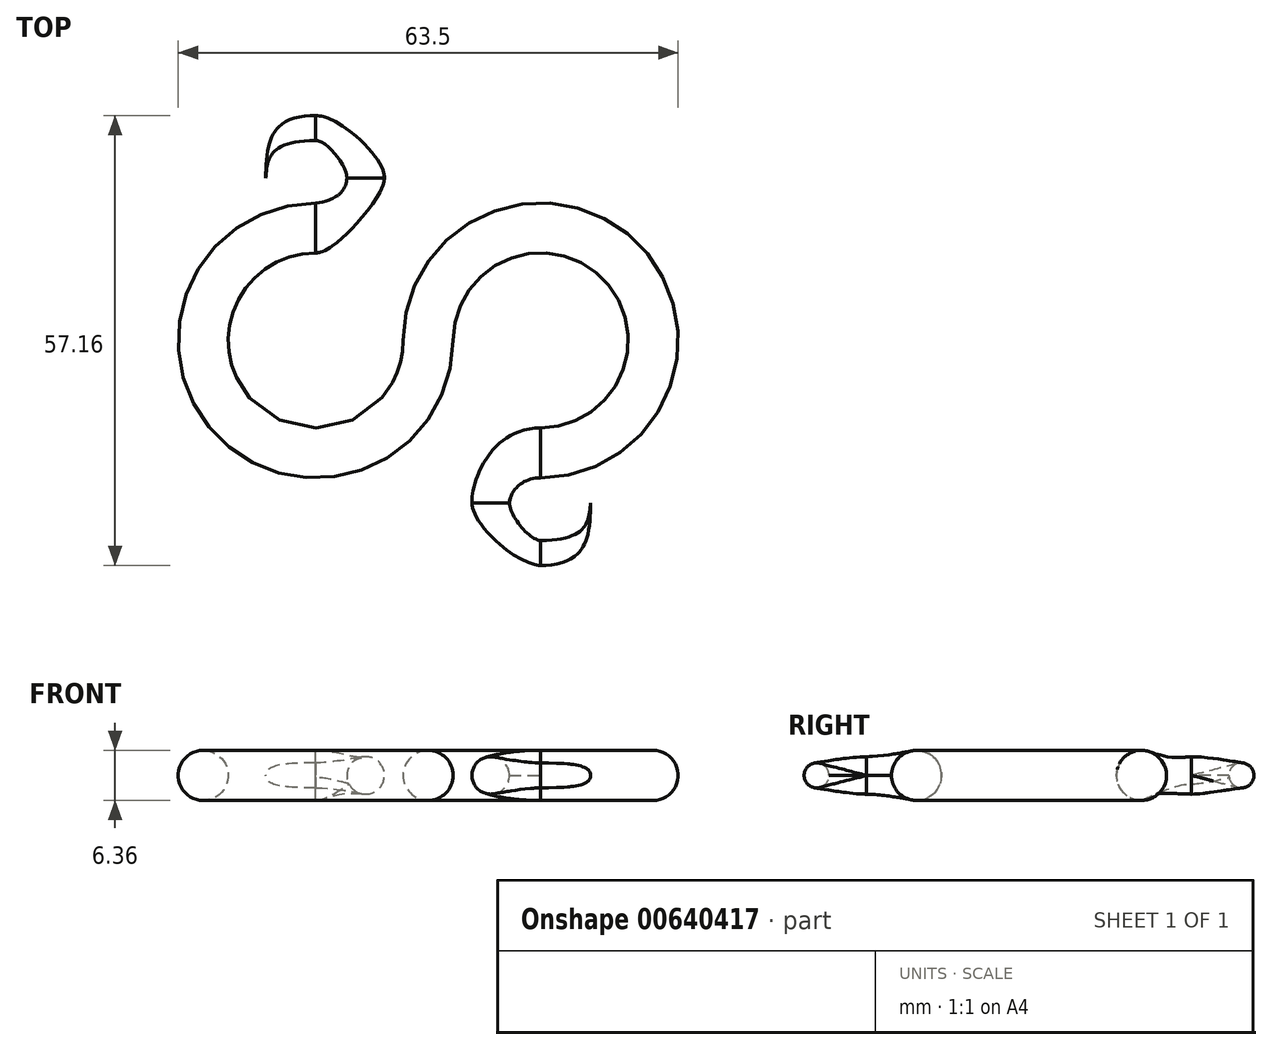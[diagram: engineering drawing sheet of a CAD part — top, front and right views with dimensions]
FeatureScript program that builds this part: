
annotation { "Feature Type Name" : "Feature", "Feature Type Description" : "" }
export const myFeature = defineFeature(function(context is Context, id is Id, definition is map)
    precondition{}
    {
        {
            var Q0;
            Q0=qCreatedBy(makeId("Top.planeOp"),FACE);
            var sketch = newSketch(context, id + "F0", { "sketchPlane" : qUnion([Q0])});
            skArc(sketch, "E0", {"start": v(0, -14.29) * mm, "mid": v(-6.35, -20.64) * mm, "end": v(0, -26.99) * mm});
            skArc(sketch, "E1", {"start": v(0, -14.29) * mm, "mid": v(10.1, 10.1) * mm, "end": v(-14.29, 0) * mm});
            skLineSegment(sketch, "E2", {"start": v(0, 0) * mm, "end": v(-14.29, 0) * mm, "construction": true});
            skLineSegment(sketch, "E3", {"start": v(0, 0) * mm, "end": v(0, -14.29) * mm, "construction": true});
            skArc(sketch, "E4", {"start": v(-28.58, 14.29) * mm, "mid": v(-38.68, -10.1) * mm, "end": v(-14.29, 0) * mm});
            skArc(sketch, "E5", {"start": v(-28.58, 14.29) * mm, "mid": v(-22.22, 20.64) * mm, "end": v(-28.57, 26.99) * mm});
            skArc(sketch, "E6", {"start": v(0, -26.99) * mm, "mid": v(4.5, -25.13) * mm, "end": v(6.35, -20.64) * mm});
            skArc(sketch, "E7", {"start": v(-28.57, 26.99) * mm, "mid": v(-33.07, 25.13) * mm, "end": v(-34.93, 20.64) * mm});
            skLineSegment(sketch, "E8", {"start": v(0, -20.64) * mm, "end": v(6.35, -20.64) * mm, "construction": true});
            skLineSegment(sketch, "E9", {"start": v(0, -20.64) * mm, "end": v(0, -26.99) * mm, "construction": true});
            skLineSegment(sketch, "E10", {"start": v(-34.92, 20.64) * mm, "end": v(-28.58, 20.64) * mm, "construction": true});
            skLineSegment(sketch, "E11", {"start": v(-28.58, 26.99) * mm, "end": v(-28.57, 20.64) * mm, "construction": true});
            skSolve(sketch);
        }
        {
            var Q0;
            Q0=sQuery(id+"F0.wireOp",EDGE,"E0");
            cPlane(context, id + "F1", {"entities" : qUnion([Q0]), "cplaneType" : CPlaneType.MID_PLANE, "offset" : 25.4 * mm, "width" : 152.4 * mm, "height" : 152.4 * mm});
        }
        {
            var Q0;
            Q0=qCreatedBy(makeId("Right.planeOp"),FACE);
            var sketch = newSketch(context, id + "F2", { "sketchPlane" : qUnion([Q0])});
            skCircle(sketch, "E12", {"center": v(-14.29, 0) * mm, "radius": 3.17 * mm});
            skCircle(sketch, "E13", {"center": v(-26.99, 0) * mm, "radius": 1.59 * mm});
            skSolve(sketch);
        }
        {
            var Q0;
            Q0=qCreatedBy(id+"F1.planeOp",FACE);
            var sketch = newSketch(context, id + "F3", { "sketchPlane" : qUnion([Q0])});
            skCircle(sketch, "E14", {"center": v(-6.35, 0) * mm, "radius": 2.38 * mm});
            skSolve(sketch);
        }
        {
            var Q0;
            Q0=makeQuery(id+"F3.imprint","IMPRINT",FACE,{"disambiguationData":[TD([[makeQuery(id+"F3.imprint","IMPRINT",EDGE,{"derivedFrom":sQuery(id+"F3.wireOp",EDGE,"E14")}),1.0]])]});
            var Q1;
            Q1=makeQuery(id+"F2.imprint","IMPRINT",FACE,{"disambiguationData":[TD([[makeQuery(id+"F2.imprint","IMPRINT",EDGE,{"derivedFrom":sQuery(id+"F2.wireOp",EDGE,"E13")}),1.0]])]});
            var Q2;
            Q2=sQuery(id+"F0.wireOp",EDGE,"E0");
            loft(context, id + "F4", {"startCondition" : LoftEndDerivativeType.NORMAL_TO_PROFILE, "startMagnitude" : 1, "endCondition" : LoftEndDerivativeType.NORMAL_TO_PROFILE, "endMagnitude" : 1, "sheetProfilesArray" : [{ "sheetProfileEntities" : qUnion([Q0]) }, { "sheetProfileEntities" : qUnion([Q1]) }], "guidesArray" : [{ "guideEntities" : qUnion([Q2]), "guideDerivativeType" : LoftGuideDerivativeType.DEFAULT, "guideDerivativeMagnitude" : 1 }]});
        }
        {
            var Q1;
            Q1=makeQuery(id+"F4.opLoft","CAP_FACE",FACE,{"disambiguationData":[OSD([makeQuery(id+"F3.imprint","IMPRINT",FACE,{"disambiguationData":[TD([[makeQuery(id+"F3.imprint","IMPRINT",EDGE,{"derivedFrom":sQuery(id+"F3.wireOp",EDGE,"E14")}),1.0]])]})])],"isStart":true});
            var Q2;
            Q2=makeQuery(id+"F2.imprint","IMPRINT",FACE,{"disambiguationData":[TD([[makeQuery(id+"F2.imprint","IMPRINT",EDGE,{"derivedFrom":sQuery(id+"F2.wireOp",EDGE,"E12")}),1.0]])]});
            loft(context, id + "F5", {"operationType" : NewBodyOperationType.ADD, "startCondition" : LoftEndDerivativeType.NORMAL_TO_PROFILE, "startMagnitude" : 1, "endCondition" : LoftEndDerivativeType.NORMAL_TO_PROFILE, "endMagnitude" : 2, "sheetProfilesArray" : [{ "sheetProfileEntities" : qUnion([Q1]) }, { "sheetProfileEntities" : qUnion([Q2]) }]});
        }
        {
            var Q0;
            Q0=makeQuery(id+"F2.imprint","IMPRINT",FACE,{"disambiguationData":[TD([[makeQuery(id+"F2.imprint","IMPRINT",EDGE,{"derivedFrom":sQuery(id+"F2.wireOp",EDGE,"E13")}),1.0]])]});
            var Q1;
            Q1=sQuery(id+"F0.wireOp",VERTEX,"E6.end");
            loft(context, id + "F6", {"operationType" : NewBodyOperationType.ADD, "startCondition" : LoftEndDerivativeType.NORMAL_TO_PROFILE, "startMagnitude" : 2.75, "sheetProfilesArray" : [{ "sheetProfileEntities" : qUnion([Q0]) }, { "sheetProfileEntities" : qUnion([Q1]) }]});
        }
        {
            var Q0;
            Q0=sQuery(id+"F0.wireOp",EDGE,"E5");
            cPlane(context, id + "F7", {"entities" : qUnion([Q0]), "cplaneType" : CPlaneType.MID_PLANE, "offset" : 25.4 * mm, "width" : 152.4 * mm, "height" : 152.4 * mm});
        }
        {
            var Q0;
            Q0=qCreatedBy(makeId("Right.planeOp"),FACE);
            cPlane(context, id + "F8", {"entities" : qUnion([Q0]), "cplaneType" : CPlaneType.OFFSET, "offset" : 28.57 * mm, "oppositeDirection" : true, "width" : 152.4 * mm, "height" : 152.4 * mm});
        }
        {
            var Q0;
            Q0=qCreatedBy(id+"F8.planeOp",FACE);
            var sketch = newSketch(context, id + "F9", { "sketchPlane" : qUnion([Q0])});
            skCircle(sketch, "E15", {"center": v(14.29, 0) * mm, "radius": 3.17 * mm});
            skCircle(sketch, "E16", {"center": v(26.99, 0) * mm, "radius": 1.59 * mm});
            skSolve(sketch);
        }
        {
            var Q0;
            Q0=makeQuery(id+"F2.imprint","IMPRINT",FACE,{"disambiguationData":[TD([[makeQuery(id+"F2.imprint","IMPRINT",EDGE,{"derivedFrom":sQuery(id+"F2.wireOp",EDGE,"E12")}),1.0]])]});
            var Q1;
            Q1=makeQuery(id+"F9.imprint","IMPRINT",FACE,{"disambiguationData":[TD([[makeQuery(id+"F9.imprint","IMPRINT",EDGE,{"derivedFrom":sQuery(id+"F9.wireOp",EDGE,"E15")}),1.0]])]});
            var Q2;
            Q2=sQuery(id+"F0.wireOp",EDGE,"E4");
            var Q3;
            Q3=sQuery(id+"F0.wireOp",EDGE,"E1");
            sweep(context, id + "F10", {"operationType" : NewBodyOperationType.ADD, "profiles" : qUnion([Q0, Q1]), "path" : qUnion([Q2, Q3])});
        }
        {
            var Q0;
            Q0=qCreatedBy(id+"F7.planeOp",FACE);
            var sketch = newSketch(context, id + "F11", { "sketchPlane" : qUnion([Q0])});
            skCircle(sketch, "E17", {"center": v(22.23, 0) * mm, "radius": 2.38 * mm});
            skSolve(sketch);
        }
        {
            var Q0;
            Q0=makeQuery(id+"F9.imprint","IMPRINT",FACE,{"disambiguationData":[TD([[makeQuery(id+"F9.imprint","IMPRINT",EDGE,{"derivedFrom":sQuery(id+"F9.wireOp",EDGE,"E15")}),1.0]])]});
            var Q1;
            Q1=makeQuery(id+"F11.imprint","IMPRINT",FACE,{"disambiguationData":[TD([[makeQuery(id+"F11.imprint","IMPRINT",EDGE,{"derivedFrom":sQuery(id+"F11.wireOp",EDGE,"E17")}),1.0]])]});
            loft(context, id + "F12", {"operationType" : NewBodyOperationType.ADD, "startCondition" : LoftEndDerivativeType.NORMAL_TO_PROFILE, "startMagnitude" : 1, "endCondition" : LoftEndDerivativeType.NORMAL_TO_PROFILE, "endMagnitude" : 1, "sheetProfilesArray" : [{ "sheetProfileEntities" : qUnion([Q0]) }, { "sheetProfileEntities" : qUnion([Q1]) }]});
        }
        {
            var Q1;
            Q1=makeQuery(id+"F12.opLoft","CAP_FACE",FACE,{"disambiguationData":[OSD([makeQuery(id+"F11.imprint","IMPRINT",FACE,{"disambiguationData":[TD([[makeQuery(id+"F11.imprint","IMPRINT",EDGE,{"derivedFrom":sQuery(id+"F11.wireOp",EDGE,"E17")}),1.0]])]})])],"isStart":true});
            var Q2;
            Q2=makeQuery(id+"F9.imprint","IMPRINT",FACE,{"disambiguationData":[TD([[makeQuery(id+"F9.imprint","IMPRINT",EDGE,{"derivedFrom":sQuery(id+"F9.wireOp",EDGE,"E16")}),1.0]])]});
            loft(context, id + "F13", {"operationType" : NewBodyOperationType.ADD, "startCondition" : LoftEndDerivativeType.NORMAL_TO_PROFILE, "startMagnitude" : 1, "endCondition" : LoftEndDerivativeType.NORMAL_TO_PROFILE, "endMagnitude" : 1, "sheetProfilesArray" : [{ "sheetProfileEntities" : qUnion([Q1]) }, { "sheetProfileEntities" : qUnion([Q2]) }]});
        }
        {
            var Q1;
            Q1=makeQuery(id+"F9.imprint","IMPRINT",FACE,{"disambiguationData":[TD([[makeQuery(id+"F9.imprint","IMPRINT",EDGE,{"derivedFrom":sQuery(id+"F9.wireOp",EDGE,"E16")}),1.0]])]});
            var Q2;
            Q2=sQuery(id+"F0.wireOp",VERTEX,"E10.start");
            loft(context, id + "F14", {"operationType" : NewBodyOperationType.ADD, "startCondition" : LoftEndDerivativeType.NORMAL_TO_PROFILE, "startMagnitude" : 2.75, "sheetProfilesArray" : [{ "sheetProfileEntities" : qUnion([Q1]) }, { "sheetProfileEntities" : qUnion([Q2]) }]});
        }
    });
